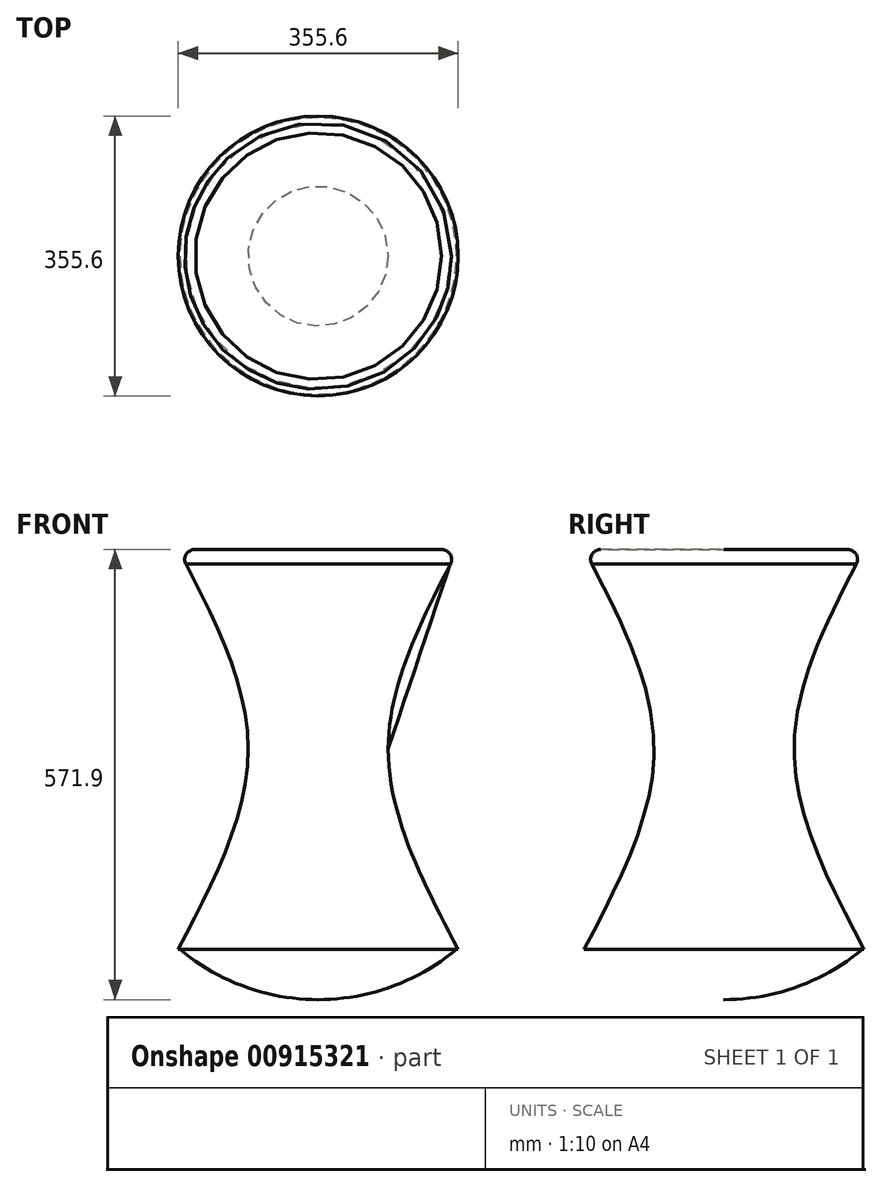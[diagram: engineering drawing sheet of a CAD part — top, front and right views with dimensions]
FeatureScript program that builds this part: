
annotation { "Feature Type Name" : "Feature", "Feature Type Description" : "" }
export const myFeature = defineFeature(function(context is Context, id is Id, definition is map)
    precondition{}
    {
        {
            var Q0;
            Q0=qCreatedBy(makeId("Right.planeOp"),FACE);
            var sketch = newSketch(context, id + "F0", { "sketchPlane" : qUnion([Q0])});
            skLineSegment(sketch, "E0", {"start": v(0, 0) * mm, "end": v(0, 508) * mm});
            skPoint(sketch, "E1", {"position": v(9.02, 0) * mm});
            skPoint(sketch, "E2", {"position": v(0, 0) * mm});
            skPoint(sketch, "E3", {"position": v(0, 254) * mm});
            skPoint(sketch, "E4", {"position": v(0, 444.5) * mm});
            skPoint(sketch, "E5", {"position": v(0, 76.2) * mm});
            skSolve(sketch);
        }
        {
            var Q0;
            Q0=qCreatedBy(makeId("Top.planeOp"),FACE);
            var sketch = newSketch(context, id + "F1", { "sketchPlane" : qUnion([Q0])});
            skCircle(sketch, "E6", {"center": v(0, 0) * mm, "radius": 177.8 * mm});
            skSolve(sketch);
        }
        {
            var Q0;
            Q0=sQuery(id+"F0.wireOp",VERTEX,"E5");
            var Q1;
            Q1=sQuery(id+"F0.wireOp",EDGE,"E0");
            cPlane(context, id + "F2", {"entities" : qUnion([Q0, Q1]), "cplaneType" : CPlaneType.CURVE_POINT, "offset" : 25.4 * mm, "width" : 152.4 * mm, "height" : 152.4 * mm});
        }
        {
            var Q0;
            Q0=sQuery(id+"F0.wireOp",EDGE,"E0");
            cPoint(context, id + "F3", {"entities" : qUnion([Q0]), "parameter" : 0.5});
        }
        {
            var Q0;
            Q0 = qCreatedBy(id + "F3" ,VERTEX);
            var Q1;
            Q1=sQuery(id+"F0.wireOp",EDGE,"E0");
            cPlane(context, id + "F4", {"entities" : qUnion([Q0, Q1]), "cplaneType" : CPlaneType.CURVE_POINT, "offset" : 25.4 * mm, "width" : 152.4 * mm, "height" : 152.4 * mm});
        }
        {
            var Q0;
            Q0=qCreatedBy(id+"F4.planeOp",FACE);
            var sketch = newSketch(context, id + "F5", { "sketchPlane" : qUnion([Q0])});
            skCircle(sketch, "E7", {"center": v(0, 0) * mm, "radius": 88.9 * mm});
            skSolve(sketch);
        }
        {
            var Q0;
            Q0=sQuery(id+"F0.wireOp",VERTEX,"E0.end");
            var Q1;
            Q1=sQuery(id+"F0.wireOp",EDGE,"E0");
            cPlane(context, id + "F6", {"entities" : qUnion([Q0, Q1]), "cplaneType" : CPlaneType.CURVE_POINT, "offset" : 25.4 * mm, "width" : 152.4 * mm, "height" : 152.4 * mm});
        }
        {
            var Q0;
            Q0=qCreatedBy(id+"F6.planeOp",FACE);
            var sketch = newSketch(context, id + "F7", { "sketchPlane" : qUnion([Q0])});
            skCircle(sketch, "E8", {"center": v(0, 0) * mm, "radius": 177.8 * mm});
            skPoint(sketch, "E9", {"position": v(175.78, 26.71) * mm});
            skSolve(sketch);
        }
        {
            var Q0;
            Q0=makeQuery(id+"F1.imprint","IMPRINT",FACE,{"disambiguationData":[TD([[makeQuery(id+"F1.imprint","IMPRINT",EDGE,{"derivedFrom":sQuery(id+"F1.wireOp",EDGE,"E6")}),1.0]])]});
            var Q1;
            Q1=makeQuery(id+"F5.imprint","IMPRINT",FACE,{"disambiguationData":[TD([[makeQuery(id+"F5.imprint","IMPRINT",EDGE,{"derivedFrom":sQuery(id+"F5.wireOp",EDGE,"E7")}),1.0]])]});
            var Q2;
            Q2=makeQuery(id+"F7.imprint","IMPRINT",FACE,{"disambiguationData":[TD([[makeQuery(id+"F7.imprint","IMPRINT",EDGE,{"derivedFrom":sQuery(id+"F7.wireOp",EDGE,"E8")}),1.0]])]});
            loft(context, id + "F8", {"sheetProfilesArray" : [{ "sheetProfileEntities" : qUnion([Q0]) }, { "sheetProfileEntities" : qUnion([Q1]) }, { "sheetProfileEntities" : qUnion([Q2]) }]});
        }
        {
            var Q0;
            Q0=makeQuery(id+"F8.opLoft","CAP_FACE",FACE,{"disambiguationData":[OSD([makeQuery(id+"F7.imprint","IMPRINT",FACE,{"disambiguationData":[TD([[makeQuery(id+"F7.imprint","IMPRINT",EDGE,{"derivedFrom":sQuery(id+"F7.wireOp",EDGE,"E8")}),1.0]])]})])],"isStart":true});
            var sketch = newSketch(context, id + "F9", { "sketchPlane" : qUnion([Q0])});
            skPoint(sketch, "E10", {"position": v(177.8, 0) * mm});
            skSolve(sketch);
        }
        {
            var Q0;
            Q0=qCreatedBy(makeId("Front.planeOp"),FACE);
            var sketch = newSketch(context, id + "F10", { "sketchPlane" : qUnion([Q0])});
            skArc(sketch, "E11", {"start": v(0, -63.9) * mm, "mid": v(93.4, -47.36) * mm, "end": v(175.6, 0) * mm});
            skLineSegment(sketch, "E12", {"start": v(0, 0) * mm, "end": v(0, -63.9) * mm});
            skPoint(sketch, "E13.orphan", {"position": v(-176.32, 0) * mm});
            skLineSegment(sketch, "E14", {"start": v(0, 0) * mm, "end": v(175.6, 0) * mm});
            skSolve(sketch);
        }
        {
            var Q0;
            Q0=makeQuery(id+"F10.imprint","IMPRINT",FACE,{"disambiguationData":[TD([[makeQuery(id+"F10.imprint","IMPRINT",EDGE,{"derivedFrom":sQuery(id+"F10.wireOp",EDGE,"E11")}),1.0]])]});
            var Q1;
            Q1=sQuery(id+"F10.wireOp",EDGE,"E12");
            revolve(context, id + "F11", {"operationType" : NewBodyOperationType.ADD, "surfaceOperationType" : NewSurfaceOperationType.NEW, "entities" : qUnion([Q0]), "axis" : qUnion([Q1]), "revolveType" : RevolveType.FULL});
        }
        {
            var Q0;
            Q0=makeQuery(id+"F8.opLoft","MID_CAP_EDGE",EDGE,{"disambiguationData":[OSD([sQuery(id+"F7.wireOp",EDGE,"E8")])],"capPos":2.0});
            fillet(context, id + "F12", {"entities" : qUnion([Q0]), "radius" : 12.7 * mm, "tangentPropagation" : true, "allowEdgeOverflow" : false});
        }
    });
